# Revit family: Faucet-Two-Handle-American_Standard-Town_Square-7455207_Series
name_source: partatom
category: Plumbing Fixtures
revit_build: Autodesk Revit 2018 (Build: 20170223_1515(x64)
units: mm (PartAtom-declared; Revit-internal decimal feet)

## family parameters
Always vertical = No
Cut with Voids When Loaded = No
OmniClass Number = 23.45.55.17
OmniClass Title = Mixing Faucets
Part Type = Normal
Room Calculation Point = No
Round Connector Dimension = Use Diameter
Shared = Yes
Work Plane-Based = Yes

## types (4) — shared parameters
ADA Compliant = Yes
Assembly Code = D2020300
CEC Compliant = Yes
CW Connection = Yes
CWFU = 1.5
CalGreen Compliant = Yes
Cold Water Connection Diameter = 1/2"
Compliance Certifications = These products meet or exceed the following codes and standards: ANSI A117.1, ASME A112.18.1, CSA B125.1,NSF 61/Section 9,NSF 372
Default Elevation = 0"
Description = Town Square® S 4-Inch Centerset 2-Handle Bathroom Faucet 1.2 gpm/4.5 L/min With Lever Handles
Flow Rate = 1.2 gpm (4.5 L/min)
HW Connection = Yes
HWFU = 1.5
Height = 4 3/8"
Hot Water Connection Diameter = 1"
Installation Type = Deck Mounted
Length = 9 7/16"
Manufacturer = American Standard
Metal push pop-up drain = Yes
Pop Up Drain Depth = 4"
Pop Up Drain Width = 4"
Product Documentation Link = https://americanstandard.box.com
Product Page URL = https://www.americanstandard-us.com
Revised Date = 08/14/2022
URL = https://www.americanstandard-us.com
Vent Connection = No
WFU = 2
Warranty Information = Limited Lifetime Function and Finish Warranty
Waste Connection = No
Width = 2 1/2"

## per-type parameters (varying)
| type | Finish | Material |
| 7455207.002 | Brass-American Standard-002-Polished Chrome | Brass-American Standard-002-Polished Chrome |
| 7455207.013 | Brass-American Standard-013-Polished Nickel | Brass-American Standard-013-Polished Nickel |
| 7455207.278 | Brass-American Standard-278-Legacy Bronze | Brass-American Standard-278-Legacy Bronze |
| 7455207.295 | Brass-American Standard-295-Satin Nickel | Brass-American Standard-295-Satin Nickel |

note: column(s) folded — value = type name in every type: Model

## geometry (parser evidence)
native form markers: Sweep x5
no freeform markers — native parametric forms only
